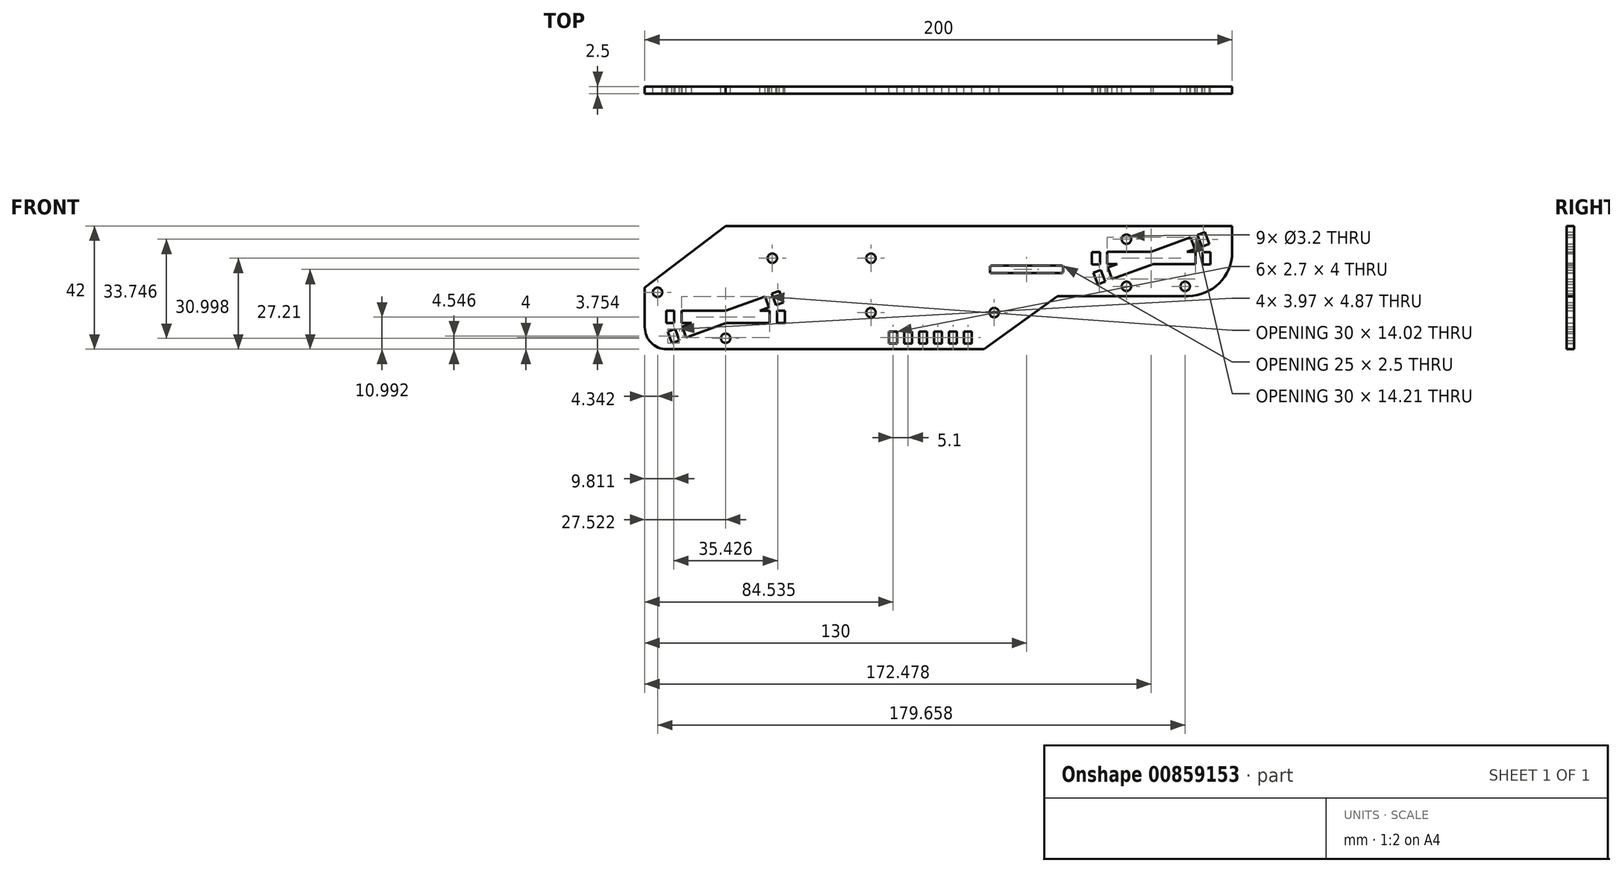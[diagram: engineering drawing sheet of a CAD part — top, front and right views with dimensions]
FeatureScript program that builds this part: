
annotation { "Feature Type Name" : "Feature", "Feature Type Description" : "" }
export const myFeature = defineFeature(function(context is Context, id is Id, definition is map)
    precondition{}
    {
        {
            var Q0;
            Q0=qCreatedBy(makeId("Front.planeOp"),FACE);
            var sketch = newSketch(context, id + "F0", { "sketchPlane" : qUnion([Q0])});
            skLineSegment(sketch, "E0", {"start": v(0, 94.2) * mm, "end": v(0, -106.67) * mm, "construction": true});
            skLineSegment(sketch, "E1", {"start": v(-120.46, 0) * mm, "end": v(57.48, 0) * mm, "construction": true});
            skLineSegment(sketch, "E2.bottom", {"start": v(-100, 0) * mm, "end": v(0, 0) * mm});
            skLineSegment(sketch, "E2.top", {"start": v(-92.5, -21) * mm, "end": v(0, -21) * mm});
            skLineSegment(sketch, "E2.left", {"start": v(-100, 0) * mm, "end": v(-100, -13.5) * mm});
            skLineSegment(sketch, "E2.right", {"start": v(0, 0) * mm, "end": v(0, -21) * mm});
            skLineSegment(sketch, "E3.bottom", {"start": v(0, 21) * mm, "end": v(100, 21) * mm});
            skLineSegment(sketch, "E3.top", {"start": v(0, 0) * mm, "end": v(100, 0) * mm});
            skLineSegment(sketch, "E3.left", {"start": v(0, 21) * mm, "end": v(0, 0) * mm});
            skLineSegment(sketch, "E3.right", {"start": v(100, 21) * mm, "end": v(100, 12.13) * mm});
            skLineSegment(sketch, "E4", {"start": v(0, -21) * mm, "end": v(15.5, -21) * mm});
            skLineSegment(sketch, "E5", {"start": v(15.5, -21) * mm, "end": v(40.59, -2.87) * mm});
            skLineSegment(sketch, "E6", {"start": v(0, 21) * mm, "end": v(-15.5, 21) * mm});
            skLineSegment(sketch, "E7", {"start": v(-87.48, 61.82) * mm, "end": v(-87.48, -70.1) * mm, "construction": true});
            skLineSegment(sketch, "E8", {"start": v(-57.48, 61.19) * mm, "end": v(-57.48, -73.28) * mm, "construction": true});
            skLineSegment(sketch, "E9.MirrorCS", {"start": v(57.48, 61.19) * mm, "end": v(57.48, -73.28) * mm, "construction": true});
            skLineSegment(sketch, "E10.MirrorCS", {"start": v(87.48, 61.82) * mm, "end": v(87.48, -70.1) * mm, "construction": true});
            skLineSegment(sketch, "E11", {"start": v(-129.62, -10) * mm, "end": v(109.07, -10) * mm, "construction": true});
            skLineSegment(sketch, "E12.MirrorCS", {"start": v(-129.62, 10) * mm, "end": v(109.07, 10) * mm, "construction": true});
            skLineSegment(sketch, "E13.bottom", {"start": v(57.48, 12.2) * mm, "end": v(87.48, 12.2) * mm});
            skLineSegment(sketch, "E13.top", {"start": v(57.48, 8) * mm, "end": v(87.48, 8) * mm});
            skLineSegment(sketch, "E13.left", {"start": v(57.48, 12.2) * mm, "end": v(57.48, 8) * mm});
            skLineSegment(sketch, "E13.right", {"start": v(87.48, 12.2) * mm, "end": v(87.48, 8) * mm});
            skLineSegment(sketch, "E14", {"start": v(-15.5, 51.3) * mm, "end": v(-15.5, -33.48) * mm, "construction": true});
            skLineSegment(sketch, "E15", {"start": v(-15.5, -33.48) * mm, "end": v(15.5, -33.48) * mm, "construction": true});
            skLineSegment(sketch, "E16", {"start": v(15.5, -33.48) * mm, "end": v(15.5, 51.3) * mm, "construction": true});
            skLineSegment(sketch, "E17", {"start": v(15.5, 51.3) * mm, "end": v(-15.5, 51.3) * mm, "construction": true});
            skLineSegment(sketch, "E18.bottom", {"start": v(-15.5, 55) * mm, "end": v(54.5, 55) * mm, "construction": true});
            skLineSegment(sketch, "E18.top", {"start": v(-15.5, 21) * mm, "end": v(54.5, 21) * mm, "construction": true});
            skLineSegment(sketch, "E18.left", {"start": v(-15.5, 55) * mm, "end": v(-15.5, 21) * mm, "construction": true});
            skLineSegment(sketch, "E18.right", {"start": v(54.5, 55) * mm, "end": v(54.5, 21) * mm, "construction": true});
            skLineSegment(sketch, "E19.bottom", {"start": v(-86.58, 21.3) * mm, "end": v(-56.58, 21.3) * mm, "construction": true});
            skLineSegment(sketch, "E19.top", {"start": v(-86.58, -7.7) * mm, "end": v(-56.58, -7.7) * mm, "construction": true});
            skLineSegment(sketch, "E19.left", {"start": v(-86.58, 21.3) * mm, "end": v(-86.58, -7.7) * mm, "construction": true});
            skLineSegment(sketch, "E19.right", {"start": v(-56.58, 21.3) * mm, "end": v(-56.58, -7.7) * mm, "construction": true});
            skLineSegment(sketch, "E20", {"start": v(-100, 0) * mm, "end": v(-72.45, 21) * mm});
            skLineSegment(sketch, "E21", {"start": v(-15.5, 21) * mm, "end": v(-72.45, 21) * mm});
            skLineSegment(sketch, "E22", {"start": v(-72.48, 50.73) * mm, "end": v(-72.48, -51.22) * mm, "construction": true});
            skLineSegment(sketch, "E23", {"start": v(-86.23, 27.78) * mm, "end": v(-72.48, -10) * mm, "construction": true});
            skLineSegment(sketch, "E24.MirrorCS", {"start": v(-86.23, -47.78) * mm, "end": v(-72.48, -10) * mm, "construction": true});
            skLineSegment(sketch, "E25.MirrorCS", {"start": v(-72.48, -70.73) * mm, "end": v(-72.48, 31.22) * mm, "construction": true});
            skLineSegment(sketch, "E26.MirrorCS", {"start": v(-58.73, 27.78) * mm, "end": v(-72.48, -10) * mm, "construction": true});
            skLineSegment(sketch, "E27.MirrorCS", {"start": v(-58.73, -47.78) * mm, "end": v(-72.48, -10) * mm, "construction": true});
            skLineSegment(sketch, "E28", {"start": v(-71.17, 30.28) * mm, "end": v(-49.8, -28.47) * mm, "construction": true});
            skLineSegment(sketch, "E29.MirrorCS", {"start": v(-99.37, 20.02) * mm, "end": v(-77.98, -38.73) * mm, "construction": true});
            skLineSegment(sketch, "E30", {"start": v(54.98, 12.1) * mm, "end": v(52.28, 12.1) * mm});
            skLineSegment(sketch, "E31", {"start": v(52.28, 12.1) * mm, "end": v(52.28, 7.9) * mm});
            skLineSegment(sketch, "E32", {"start": v(52.28, 7.9) * mm, "end": v(54.98, 7.9) * mm});
            skLineSegment(sketch, "E33", {"start": v(54.98, 7.9) * mm, "end": v(54.98, 12.1) * mm});
            skLineSegment(sketch, "E34", {"start": v(72.48, 37.02) * mm, "end": v(72.48, -16.38) * mm, "construction": true});
            skLineSegment(sketch, "E35.MirrorCS", {"start": v(92.68, 12.1) * mm, "end": v(92.68, 7.9) * mm});
            skLineSegment(sketch, "E36.MirrorCS", {"start": v(89.98, 12.1) * mm, "end": v(92.68, 12.1) * mm});
            skLineSegment(sketch, "E37.MirrorCS", {"start": v(89.98, 7.9) * mm, "end": v(89.98, 12.1) * mm});
            skLineSegment(sketch, "E38.MirrorCS", {"start": v(92.68, 7.9) * mm, "end": v(89.98, 7.9) * mm});
            skLineSegment(sketch, "E39.bottom", {"start": v(-87.48, -7.9) * mm, "end": v(-57.48, -7.9) * mm});
            skLineSegment(sketch, "E39.top", {"start": v(-87.48, -12.1) * mm, "end": v(-57.48, -12.1) * mm});
            skLineSegment(sketch, "E39.left", {"start": v(-87.48, -7.9) * mm, "end": v(-87.48, -12.1) * mm});
            skLineSegment(sketch, "E39.right", {"start": v(-57.48, -7.9) * mm, "end": v(-57.48, -12.1) * mm});
            skLineSegment(sketch, "E40.bottom", {"start": v(-92.68, -7.9) * mm, "end": v(-89.98, -7.9) * mm});
            skLineSegment(sketch, "E40.top", {"start": v(-92.68, -12.1) * mm, "end": v(-89.98, -12.1) * mm});
            skLineSegment(sketch, "E40.left", {"start": v(-92.68, -7.9) * mm, "end": v(-92.68, -12.1) * mm});
            skLineSegment(sketch, "E40.right", {"start": v(-89.98, -7.9) * mm, "end": v(-89.98, -12.1) * mm});
            skLineSegment(sketch, "E41.MirrorCS", {"start": v(-52.28, -12.1) * mm, "end": v(-54.98, -12.1) * mm});
            skLineSegment(sketch, "E42.MirrorCS", {"start": v(-54.98, -7.9) * mm, "end": v(-54.98, -12.1) * mm});
            skLineSegment(sketch, "E43.MirrorCS", {"start": v(-52.28, -7.9) * mm, "end": v(-54.98, -7.9) * mm});
            skLineSegment(sketch, "E44.MirrorCS", {"start": v(-52.28, -7.9) * mm, "end": v(-52.28, -12.1) * mm});
            skLineSegment(sketch, "E45", {"start": v(59.1, 2.9) * mm, "end": v(87.3, 13.15) * mm});
            skLineSegment(sketch, "E46", {"start": v(87.3, 13.15) * mm, "end": v(85.86, 17.1) * mm});
            skLineSegment(sketch, "E47", {"start": v(59.1, 2.9) * mm, "end": v(57.66, 6.84) * mm});
            skLineSegment(sketch, "E48", {"start": v(57.66, 6.84) * mm, "end": v(85.86, 17.1) * mm});
            skLineSegment(sketch, "E49", {"start": v(58.38, 4.87) * mm, "end": v(86.57, 15.13) * mm, "construction": true});
            skLineSegment(sketch, "E50", {"start": v(71.76, 11.97) * mm, "end": v(73.2, 8.02) * mm, "construction": true});
            skLineSegment(sketch, "E51", {"start": v(72.48, 10) * mm, "end": v(70.57, 15.25) * mm, "construction": true});
            skLineSegment(sketch, "E52", {"start": v(81.78, 18.56) * mm, "end": v(83.7, 13.3) * mm, "construction": true});
            skLineSegment(sketch, "E53", {"start": v(90.74, 18.88) * mm, "end": v(92.18, 14.93) * mm});
            skLineSegment(sketch, "E54", {"start": v(92.18, 14.93) * mm, "end": v(89.64, 14) * mm});
            skLineSegment(sketch, "E55", {"start": v(89.64, 14) * mm, "end": v(88.2, 17.96) * mm});
            skLineSegment(sketch, "E56", {"start": v(88.2, 17.96) * mm, "end": v(90.74, 18.88) * mm});
            skLineSegment(sketch, "E57.MirrorCS", {"start": v(54.22, 1.12) * mm, "end": v(56.75, 2.04) * mm});
            skLineSegment(sketch, "E58.MirrorCS", {"start": v(55.32, 5.99) * mm, "end": v(52.78, 5.06) * mm});
            skLineSegment(sketch, "E59.MirrorCS", {"start": v(56.75, 2.04) * mm, "end": v(55.32, 5.99) * mm});
            skLineSegment(sketch, "E60.MirrorCS", {"start": v(52.78, 5.06) * mm, "end": v(54.22, 1.12) * mm});
            skLineSegment(sketch, "E61", {"start": v(-85.89, -17.02) * mm, "end": v(-57.7, -6.76) * mm});
            skLineSegment(sketch, "E62", {"start": v(-57.7, -6.76) * mm, "end": v(-59.07, -3) * mm});
            skLineSegment(sketch, "E63", {"start": v(-85.89, -17.02) * mm, "end": v(-87.26, -13.26) * mm});
            skLineSegment(sketch, "E64", {"start": v(-87.26, -13.26) * mm, "end": v(-59.07, -3) * mm});
            skLineSegment(sketch, "E65", {"start": v(-86.57, -15.14) * mm, "end": v(-58.38, -4.88) * mm, "construction": true});
            skLineSegment(sketch, "E66", {"start": v(-73.16, -8.13) * mm, "end": v(-71.8, -11.89) * mm, "construction": true});
            skLineSegment(sketch, "E67", {"start": v(-54.21, -1.12) * mm, "end": v(-52.78, -5.07) * mm});
            skLineSegment(sketch, "E68", {"start": v(-52.78, -5.07) * mm, "end": v(-55.31, -6) * mm});
            skLineSegment(sketch, "E69", {"start": v(-55.31, -6) * mm, "end": v(-56.75, -2.05) * mm});
            skLineSegment(sketch, "E70", {"start": v(-56.75, -2.05) * mm, "end": v(-54.21, -1.12) * mm});
            skLineSegment(sketch, "E71.MirrorCS", {"start": v(-89.64, -14.02) * mm, "end": v(-92.18, -14.94) * mm});
            skLineSegment(sketch, "E72.MirrorCS", {"start": v(-92.18, -14.94) * mm, "end": v(-90.74, -18.89) * mm});
            skLineSegment(sketch, "E73.MirrorCS", {"start": v(-88.2, -17.97) * mm, "end": v(-89.64, -14.02) * mm});
            skLineSegment(sketch, "E74.MirrorCS", {"start": v(-90.74, -18.89) * mm, "end": v(-88.2, -17.97) * mm});
            skLineSegment(sketch, "E75", {"start": v(40.59, -2.87) * mm, "end": v(85, -2.87) * mm});
            skLineSegment(sketch, "E76", {"start": v(100, -2.87) * mm, "end": v(100, 0) * mm});
            skLineSegment(sketch, "E77.trimOffspring", {"start": v(87.48, 0) * mm, "end": v(126.59, 0) * mm, "construction": true});
            skPoint(sketch, "E78.newPointA", {"position": v(100, -2.87) * mm});
            skPoint(sketch, "E78.newPointB", {"position": v(100, 0) * mm});
            skArc(sketch, "E78.filletArc", {"start": v(85, -2.87) * mm, "mid": v(95.6, 1.53) * mm, "end": v(100, 12.13) * mm});
            skPoint(sketch, "E79.visualSharp", {"position": v(-100, -21) * mm});
            skArc(sketch, "E79.filletArc", {"start": v(-100, -13.5) * mm, "mid": v(-97.8, -18.8) * mm, "end": v(-92.5, -21) * mm});
            skLineSegment(sketch, "E80.bottom", {"start": v(11.39, -15) * mm, "end": v(8.69, -15) * mm});
            skLineSegment(sketch, "E80.top", {"start": v(11.39, -19) * mm, "end": v(8.69, -19) * mm});
            skLineSegment(sketch, "E80.left", {"start": v(11.39, -15) * mm, "end": v(11.39, -19) * mm});
            skLineSegment(sketch, "E80.right", {"start": v(8.69, -15) * mm, "end": v(8.69, -19) * mm});
            skLineSegment(sketch, "E81.bottom", {"start": v(6.29, -15) * mm, "end": v(3.59, -15) * mm});
            skLineSegment(sketch, "E81.top", {"start": v(6.29, -19) * mm, "end": v(3.59, -19) * mm});
            skLineSegment(sketch, "E81.left", {"start": v(6.29, -15) * mm, "end": v(6.29, -19) * mm});
            skLineSegment(sketch, "E81.right", {"start": v(3.59, -15) * mm, "end": v(3.59, -19) * mm});
            skLineSegment(sketch, "E82.bottom", {"start": v(1.19, -15) * mm, "end": v(-1.51, -15) * mm});
            skLineSegment(sketch, "E82.top", {"start": v(1.19, -19) * mm, "end": v(-1.51, -19) * mm});
            skLineSegment(sketch, "E82.left", {"start": v(1.19, -15) * mm, "end": v(1.19, -19) * mm});
            skLineSegment(sketch, "E82.right", {"start": v(-1.51, -15) * mm, "end": v(-1.51, -19) * mm});
            skLineSegment(sketch, "E83.bottom", {"start": v(-3.91, -15) * mm, "end": v(-6.61, -15) * mm});
            skLineSegment(sketch, "E83.top", {"start": v(-3.91, -19) * mm, "end": v(-6.61, -19) * mm});
            skLineSegment(sketch, "E83.left", {"start": v(-3.91, -15) * mm, "end": v(-3.91, -19) * mm});
            skLineSegment(sketch, "E83.right", {"start": v(-6.61, -15) * mm, "end": v(-6.61, -19) * mm});
            skLineSegment(sketch, "E84.bottom", {"start": v(-9.01, -15) * mm, "end": v(-11.71, -15) * mm});
            skLineSegment(sketch, "E84.top", {"start": v(-9.01, -19) * mm, "end": v(-11.71, -19) * mm});
            skLineSegment(sketch, "E84.left", {"start": v(-9.01, -15) * mm, "end": v(-9.01, -19) * mm});
            skLineSegment(sketch, "E84.right", {"start": v(-11.71, -15) * mm, "end": v(-11.71, -19) * mm});
            skLineSegment(sketch, "E85.bottom", {"start": v(-14.11, -15) * mm, "end": v(-16.81, -15) * mm});
            skLineSegment(sketch, "E85.top", {"start": v(-14.11, -19) * mm, "end": v(-16.81, -19) * mm});
            skLineSegment(sketch, "E85.left", {"start": v(-14.11, -15) * mm, "end": v(-14.11, -19) * mm});
            skLineSegment(sketch, "E85.right", {"start": v(-16.81, -15) * mm, "end": v(-16.81, -19) * mm});
            skCircle(sketch, "E86", {"center": v(64, 16.5) * mm, "radius": 1.6 * mm});
            skCircle(sketch, "E87", {"center": v(19, -8.5) * mm, "radius": 1.6 * mm});
            skCircle(sketch, "E88", {"center": v(-23, -8.5) * mm, "radius": 1.6 * mm});
            skCircle(sketch, "E89", {"center": v(-23, 10) * mm, "radius": 1.6 * mm});
            skCircle(sketch, "E90", {"center": v(64, 0.44) * mm, "radius": 1.6 * mm});
            skCircle(sketch, "E91", {"center": v(84, 0.44) * mm, "radius": 1.6 * mm});
            skCircle(sketch, "E92", {"center": v(-72.48, -17.25) * mm, "radius": 1.6 * mm});
            skCircle(sketch, "E93", {"center": v(-56.58, 10) * mm, "radius": 1.6 * mm});
            skCircle(sketch, "E94", {"center": v(-95.66, -1.58) * mm, "radius": 1.6 * mm});
            skLineSegment(sketch, "E95.bottom", {"start": v(42, 7.46) * mm, "end": v(18, 7.46) * mm});
            skLineSegment(sketch, "E95.top", {"start": v(42, 4.96) * mm, "end": v(18, 4.96) * mm});
            skLineSegment(sketch, "E95.left", {"start": v(42.5, 6.96) * mm, "end": v(42.5, 5.46) * mm});
            skLineSegment(sketch, "E95.right", {"start": v(17.5, 6.96) * mm, "end": v(17.5, 5.46) * mm});
            skPoint(sketch, "E96.visualSharp", {"position": v(17.5, 7.46) * mm});
            skArc(sketch, "E96.filletArc", {"start": v(18, 7.46) * mm, "mid": v(17.65, 7.31) * mm, "end": v(17.5, 6.96) * mm});
            skPoint(sketch, "E97.visualSharp", {"position": v(42.5, 7.46) * mm});
            skArc(sketch, "E97.filletArc", {"start": v(42.5, 6.96) * mm, "mid": v(42.35, 7.31) * mm, "end": v(42, 7.46) * mm});
            skPoint(sketch, "E98.visualSharp", {"position": v(42.5, 4.96) * mm});
            skArc(sketch, "E98.filletArc", {"start": v(42, 4.96) * mm, "mid": v(42.35, 5.1) * mm, "end": v(42.5, 5.46) * mm});
            skPoint(sketch, "E99.visualSharp", {"position": v(17.5, 4.96) * mm});
            skArc(sketch, "E99.filletArc", {"start": v(17.5, 5.46) * mm, "mid": v(17.65, 5.1) * mm, "end": v(18, 4.96) * mm});
            skSolve(sketch);
        }
        {
            var Q0;
            Q0 = qSketchRegion(id + "F0", true);
            extrude(context, id + "F1", {"entities" : qUnion([Q0]), "depth" : 2.5 * mm, "offsetDistance" : 25 * mm});
        }
    });
